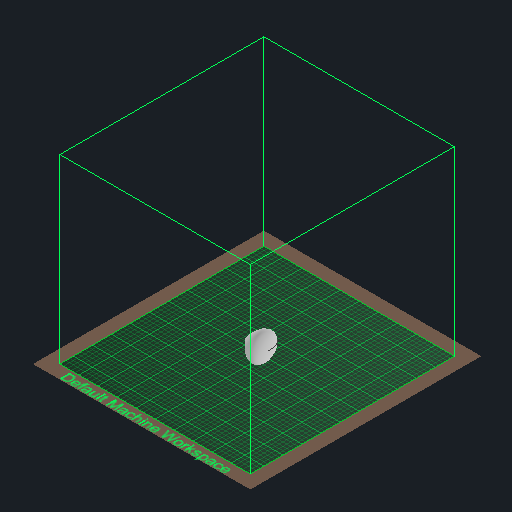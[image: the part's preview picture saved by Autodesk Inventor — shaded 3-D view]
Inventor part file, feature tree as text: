
AUTODESK INVENTOR PART (.ipt)
format: ipt  version: 2022 (Build 260153000, 153)  size: 412,160 bytes
history: native  units: in
note: dims shown in document units (in); Inventor stores cm internally (conversion verified against a paired STEP export)
features: sketch x2, revolve x1, extrude x1, other x1, projected_geometry x1
ambient origin geometry x8: Origin, YZ Plane, XZ Plane, XY Plane, X Axis, Y Axis, Z Axis, Center Point
bodies: Solid1 (feature_tree)
feature tree (6):
  revolve  "Revolution1"  Angle=90.0deg
  extrude  "Extrusion1"  [1 undecoded]
  sketch  "Sketch1"  dims[d0=0.0in d1=0.7874in d2=90.0deg]
  other  "2D Equation Curve1"
  sketch  "Sketch2"  dims[d3=5.0in d4=0.0in]
  projected_geometry  "Projected Loop1"
note: 1 required parameter value undecoded (feature->parameter linkage not recoverable at this tier; creation-order binding heuristic only, values carry confidence <= 0.55)
